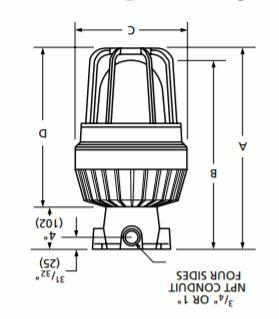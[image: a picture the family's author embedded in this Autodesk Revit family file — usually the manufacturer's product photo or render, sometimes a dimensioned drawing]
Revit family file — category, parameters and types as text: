
# Revit family: HLEMLC
name_source: partatom
category: Lighting Fixtures
revit_build: Autodesk Revit 2014 (Build: 20130308_1515(x64)
units: mm (PartAtom-declared; Revit-internal decimal feet)

## types (1)
- HLEMLC
    Apparent Load = 45 VA
    Applications = Industrial, Food Processing, Heavy Industry, Marine, Petroleum, Chemical/Plastic, Cleanroom, Paper/Textile, Iron/Steel
    CRI = 70 CRI
    Certification = CSA Listed to UL844
• CSA Listed to UL1598 Wet Location
• Wet Location listed up to 90 degrees
• Damp location listed at greater than 90 degrees mounting angle
• Class I, Division 2, Groups A, B, C & D
• IP66 with factory installed ENCG option
    Color Filter = 16777215
    Default Elevation = 48 "
    Description = The HLEML is designed to light classified areas such as paint manufacturing plants, ammunition facilities, oil and gas producing and refining plants, off-shore and dock side installations, tank farms, pipeline pumping stations and marine loading and fuel transfer terminals
    Dimming Lamp Color Temperature Shift = <None>
    Emit Shape Visible in Rendering = No
    Emit from Circle Diameter = 4 "
    Fastners = Paint - Hubbell - Light Silver
    Features = Class 1, Division 1 LED Explosion Proof

Specialized thermal management allows up to 55°C ambient
120v to 277v universal voltage drivers
Operating temperature range: -40°C to 55°C
50,000 hours to 70% initial lumens
5000˚K color temperature - crisp white light
Factory sealed
    Glass = Hubbell - Glass
    Lamp = 24 High Performanc LEDs
    Load Classification = Lighting
    Manufacturer = Hubbell Industrial Lighting
    Material Finish = Paint - Hubbell - White Texture
    Model = HLEMLC
    Photometric Web File = Generic.ies
    Power Factor = 1
    Product Documentation Link = https://hubbellcdn.com
    Product Page URL = https://www.hubbell.com
    Tilt Angle = -90.00°
    URL = https://www.hubbell.com
    Voltage = 120 V
    Warranty = 5 Year Warranty
    Watt = 45 W
    Wattage Comments = 45 Watts

## geometry (parser evidence)
native form markers: Blend x4, Sweep x4
no freeform markers — native parametric forms only
